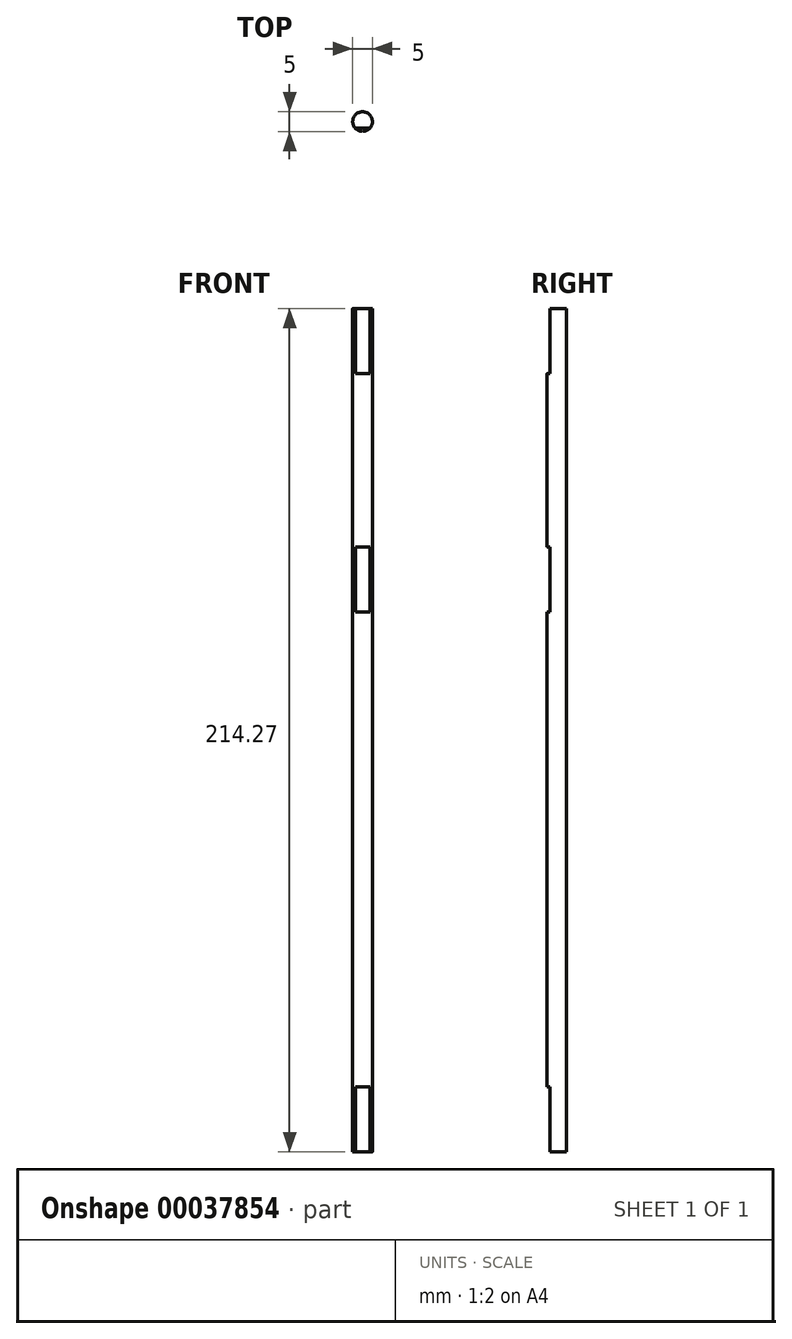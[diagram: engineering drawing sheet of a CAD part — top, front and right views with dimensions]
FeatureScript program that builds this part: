
annotation { "Feature Type Name" : "Feature", "Feature Type Description" : "" }
export const myFeature = defineFeature(function(context is Context, id is Id, definition is map)
    precondition{}
    {
        {
            var Q0;
            Q0=qCreatedBy(makeId("Top.planeOp"),FACE);
            var sketch = newSketch(context, id + "F0", { "sketchPlane" : qUnion([Q0])});
            skCircle(sketch, "E0", {"center": v(0, 0) * mm, "radius": 2.5 * mm});
            skSolve(sketch);
        }
        {
            var Q0;
            Q0 = qSketchRegion(id + "F0", true);
            extrude(context, id + "F1", {"entities" : qUnion([Q0]), "depth" : 214.27 * mm});
        }
        {
            var Q0;
            Q0=qCreatedBy(makeId("Right.planeOp"),FACE);
            var sketch = newSketch(context, id + "F2", { "sketchPlane" : qUnion([Q0])});
            skLineSegment(sketch, "E1.bottom", {"start": v(-1.7, 0) * mm, "end": v(-2.5, 0) * mm});
            skLineSegment(sketch, "E1.top", {"start": v(-1.7, 16.53) * mm, "end": v(-2.5, 16.53) * mm});
            skLineSegment(sketch, "E1.left", {"start": v(-1.7, 0) * mm, "end": v(-1.7, 16.53) * mm});
            skLineSegment(sketch, "E1.right", {"start": v(-2.5, 0) * mm, "end": v(-2.5, 16.53) * mm});
            skLineSegment(sketch, "E2", {"start": v(-1.7, 0) * mm, "end": v(0, 0) * mm});
            skLineSegment(sketch, "E3.bottom", {"start": v(-1.7, 214.27) * mm, "end": v(-2.5, 214.27) * mm});
            skLineSegment(sketch, "E3.top", {"start": v(-1.7, 197.75) * mm, "end": v(-2.5, 197.75) * mm});
            skLineSegment(sketch, "E3.left", {"start": v(-1.7, 214.27) * mm, "end": v(-1.7, 197.75) * mm});
            skLineSegment(sketch, "E3.right", {"start": v(-2.5, 214.27) * mm, "end": v(-2.5, 197.75) * mm});
            skLineSegment(sketch, "E4", {"start": v(-1.7, 214.27) * mm, "end": v(0, 214.27) * mm});
            skLineSegment(sketch, "E5.bottom", {"start": v(-2.5, 153.73) * mm, "end": v(-1.7, 153.73) * mm});
            skLineSegment(sketch, "E5.top", {"start": v(-2.5, 137.2) * mm, "end": v(-1.7, 137.2) * mm});
            skLineSegment(sketch, "E5.left", {"start": v(-2.5, 153.73) * mm, "end": v(-2.5, 137.2) * mm});
            skLineSegment(sketch, "E5.right", {"start": v(-1.7, 153.73) * mm, "end": v(-1.7, 137.2) * mm});
            skLineSegment(sketch, "E6", {"start": v(-1.7, 16.53) * mm, "end": v(-1.7, 137.2) * mm});
            skSolve(sketch);
        }
        {
            var Q0;
            Q0 = qSketchRegion(id + "F2", true);
            var Q1;
            Q1=makeQuery(id+"F1.opExtrude","SWEPT_FACE",FACE,{"disambiguationData":[OSD([sQuery(id+"F0.wireOp",EDGE,"E0")])]});
            var Q2;
            Q2=makeQuery(id+"F1.opExtrude","SWEPT_FACE",FACE,{"disambiguationData":[OSD([sQuery(id+"F0.wireOp",EDGE,"E0")])]});
            extrude(context, id + "F3", {"entities" : qUnion([Q0]), "operationType" : NewBodyOperationType.REMOVE, "endBound" : BoundingType.UP_TO_SURFACE, "oppositeDirection" : true, "endBoundEntityFace" : qUnion([Q1]), "depth" : 25.4 * mm, "hasSecondDirection" : true, "secondDirectionBound" : SecondDirectionBoundingType.UP_TO_SURFACE, "secondDirectionOppositeDirection" : false, "secondDirectionBoundEntityFace" : qUnion([Q2]), "secondDirectionDepth" : 25.4 * mm});
        }
    });
